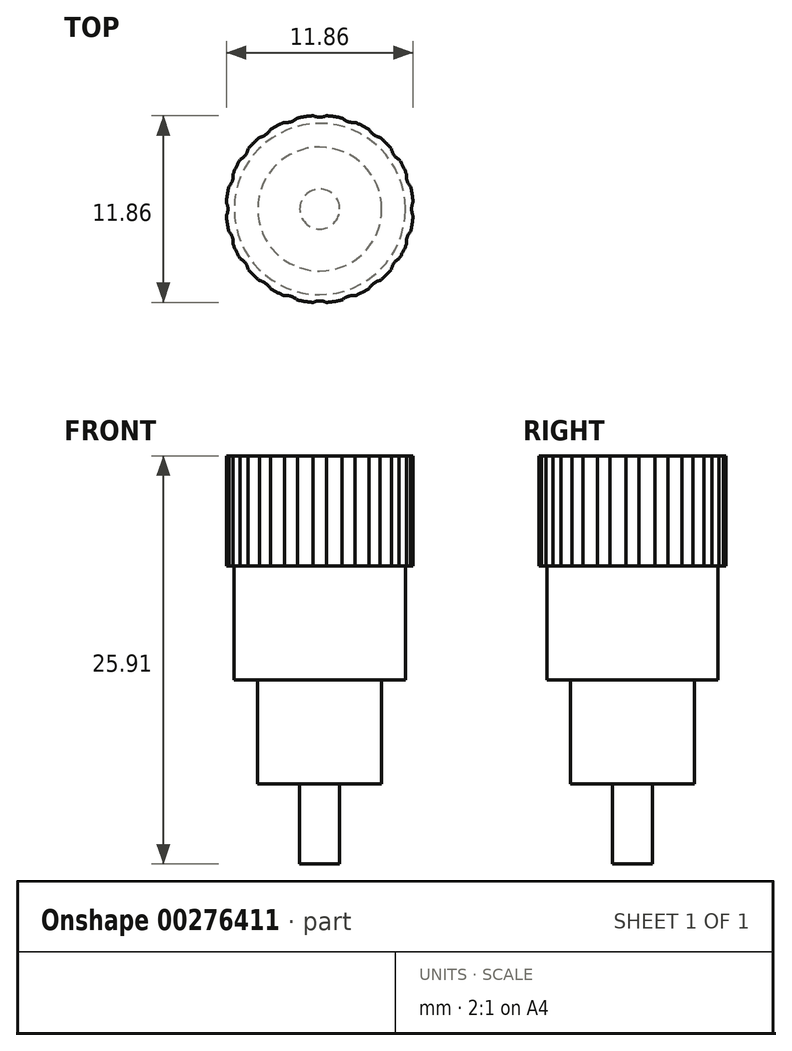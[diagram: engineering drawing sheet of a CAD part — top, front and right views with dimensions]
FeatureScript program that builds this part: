
annotation { "Feature Type Name" : "Feature", "Feature Type Description" : "" }
export const myFeature = defineFeature(function(context is Context, id is Id, definition is map)
    precondition{}
    {
        {
            var Q0;
            Q0=qCreatedBy(makeId("Front.planeOp"),FACE);
            var sketch = newSketch(context, id + "F0", { "sketchPlane" : qUnion([Q0])});
            skLineSegment(sketch, "E0", {"start": v(0, -6.98) * mm, "end": v(0, 66.06) * mm, "construction": true});
            skLineSegment(sketch, "E1", {"start": v(0, 20.83) * mm, "end": v(5.94, 20.83) * mm});
            skLineSegment(sketch, "E2", {"start": v(5.94, 20.83) * mm, "end": v(5.94, 13.84) * mm});
            skLineSegment(sketch, "E3", {"start": v(5.94, 13.84) * mm, "end": v(5.44, 13.84) * mm});
            skLineSegment(sketch, "E4", {"start": v(5.44, 13.84) * mm, "end": v(5.44, 6.6) * mm});
            skLineSegment(sketch, "E5", {"start": v(5.44, 6.6) * mm, "end": v(3.94, 6.6) * mm});
            skLineSegment(sketch, "E6", {"start": v(3.94, 6.6) * mm, "end": v(3.94, 0) * mm});
            skLineSegment(sketch, "E7", {"start": v(3.94, 0) * mm, "end": v(1.27, 0) * mm});
            skLineSegment(sketch, "E8", {"start": v(1.27, 0) * mm, "end": v(1.27, -5.08) * mm});
            skLineSegment(sketch, "E9", {"start": v(1.27, -5.08) * mm, "end": v(0, -5.08) * mm});
            skLineSegment(sketch, "E10", {"start": v(0, -5.08) * mm, "end": v(0, 20.83) * mm});
            skSolve(sketch);
        }
        {
            var Q0;
            Q0 = qSketchRegion(id + "F0", true);
            var Q1;
            Q1=sQuery(id+"F0.wireOp",EDGE,"E0");
            revolve(context, id + "F1", {"entities" : qUnion([Q0]), "axis" : qUnion([Q1]), "revolveType" : RevolveType.FULL});
        }
        {
            var Q0;
            Q0=makeQuery(id+"F1.opRevolve","SWEPT_FACE",FACE,{"disambiguationData":[OSD([sQuery(id+"F0.wireOp",EDGE,"E1")])]});
            var sketch = newSketch(context, id + "F2", { "sketchPlane" : qUnion([Q0])});
            skArc(sketch, "E11", {"start": v(0.43, 5.93) * mm, "mid": v(0, 5.83) * mm, "end": v(-0.43, 5.93) * mm});
            skArc(sketch, "E12", {"start": v(-0.43, 5.93) * mm, "mid": v(0, 5.94) * mm, "end": v(0.43, 5.93) * mm});
            skArc(sketch, "E13.1.0", {"start": v(-2.24, 5.5) * mm, "mid": v(-1.84, 5.65) * mm, "end": v(-1.43, 5.77) * mm});
            skArc(sketch, "E13.1.1", {"start": v(-1.43, 5.77) * mm, "mid": v(-1.8, 5.55) * mm, "end": v(-2.24, 5.5) * mm});
            skArc(sketch, "E13.2.0", {"start": v(-3.83, 4.54) * mm, "mid": v(-3.5, 4.8) * mm, "end": v(-3.14, 5.05) * mm});
            skArc(sketch, "E13.2.1", {"start": v(-3.14, 5.05) * mm, "mid": v(-3.43, 4.72) * mm, "end": v(-3.83, 4.54) * mm});
            skArc(sketch, "E13.3.0", {"start": v(-5.05, 3.14) * mm, "mid": v(-4.8, 3.5) * mm, "end": v(-4.54, 3.83) * mm});
            skArc(sketch, "E13.3.1", {"start": v(-4.54, 3.83) * mm, "mid": v(-4.72, 3.43) * mm, "end": v(-5.05, 3.14) * mm});
            skArc(sketch, "E13.4.0", {"start": v(-5.77, 1.43) * mm, "mid": v(-5.65, 1.84) * mm, "end": v(-5.5, 2.24) * mm});
            skArc(sketch, "E13.4.1", {"start": v(-5.5, 2.24) * mm, "mid": v(-5.55, 1.8) * mm, "end": v(-5.77, 1.43) * mm});
            skArc(sketch, "E13.5.0", {"start": v(-5.93, -0.43) * mm, "mid": v(-5.94, 0) * mm, "end": v(-5.93, 0.43) * mm});
            skArc(sketch, "E13.5.1", {"start": v(-5.93, 0.43) * mm, "mid": v(-5.83, 0) * mm, "end": v(-5.93, -0.43) * mm});
            skArc(sketch, "E13.6.0", {"start": v(-5.5, -2.24) * mm, "mid": v(-5.65, -1.84) * mm, "end": v(-5.77, -1.43) * mm});
            skArc(sketch, "E13.6.1", {"start": v(-5.77, -1.43) * mm, "mid": v(-5.55, -1.8) * mm, "end": v(-5.5, -2.24) * mm});
            skArc(sketch, "E13.7.0", {"start": v(-4.54, -3.83) * mm, "mid": v(-4.8, -3.5) * mm, "end": v(-5.05, -3.14) * mm});
            skArc(sketch, "E13.7.1", {"start": v(-5.05, -3.14) * mm, "mid": v(-4.72, -3.43) * mm, "end": v(-4.54, -3.83) * mm});
            skArc(sketch, "E13.8.0", {"start": v(-3.14, -5.05) * mm, "mid": v(-3.5, -4.8) * mm, "end": v(-3.83, -4.54) * mm});
            skArc(sketch, "E13.8.1", {"start": v(-3.83, -4.54) * mm, "mid": v(-3.43, -4.72) * mm, "end": v(-3.14, -5.05) * mm});
            skArc(sketch, "E13.9.0", {"start": v(-1.43, -5.77) * mm, "mid": v(-1.84, -5.65) * mm, "end": v(-2.24, -5.5) * mm});
            skArc(sketch, "E13.9.1", {"start": v(-2.24, -5.5) * mm, "mid": v(-1.8, -5.55) * mm, "end": v(-1.43, -5.77) * mm});
            skArc(sketch, "E13.10.0", {"start": v(0.43, -5.93) * mm, "mid": v(0, -5.94) * mm, "end": v(-0.43, -5.93) * mm});
            skArc(sketch, "E13.10.1", {"start": v(-0.43, -5.93) * mm, "mid": v(0, -5.83) * mm, "end": v(0.43, -5.93) * mm});
            skArc(sketch, "E13.11.0", {"start": v(2.24, -5.5) * mm, "mid": v(1.84, -5.65) * mm, "end": v(1.43, -5.77) * mm});
            skArc(sketch, "E13.11.1", {"start": v(1.43, -5.77) * mm, "mid": v(1.8, -5.55) * mm, "end": v(2.24, -5.5) * mm});
            skArc(sketch, "E13.12.0", {"start": v(3.83, -4.54) * mm, "mid": v(3.5, -4.8) * mm, "end": v(3.14, -5.05) * mm});
            skArc(sketch, "E13.12.1", {"start": v(3.14, -5.05) * mm, "mid": v(3.43, -4.72) * mm, "end": v(3.83, -4.54) * mm});
            skArc(sketch, "E13.13.0", {"start": v(5.05, -3.14) * mm, "mid": v(4.8, -3.5) * mm, "end": v(4.54, -3.83) * mm});
            skArc(sketch, "E13.13.1", {"start": v(4.54, -3.83) * mm, "mid": v(4.72, -3.43) * mm, "end": v(5.05, -3.14) * mm});
            skArc(sketch, "E13.14.0", {"start": v(5.77, -1.43) * mm, "mid": v(5.65, -1.84) * mm, "end": v(5.5, -2.24) * mm});
            skArc(sketch, "E13.14.1", {"start": v(5.5, -2.24) * mm, "mid": v(5.55, -1.8) * mm, "end": v(5.77, -1.43) * mm});
            skArc(sketch, "E13.15.0", {"start": v(5.93, 0.43) * mm, "mid": v(5.94, 0) * mm, "end": v(5.93, -0.43) * mm});
            skArc(sketch, "E13.15.1", {"start": v(5.93, -0.43) * mm, "mid": v(5.83, 0) * mm, "end": v(5.93, 0.43) * mm});
            skArc(sketch, "E13.16.0", {"start": v(5.5, 2.24) * mm, "mid": v(5.65, 1.84) * mm, "end": v(5.77, 1.43) * mm});
            skArc(sketch, "E13.16.1", {"start": v(5.77, 1.43) * mm, "mid": v(5.55, 1.8) * mm, "end": v(5.5, 2.24) * mm});
            skArc(sketch, "E13.17.0", {"start": v(4.54, 3.83) * mm, "mid": v(4.8, 3.5) * mm, "end": v(5.05, 3.14) * mm});
            skArc(sketch, "E13.17.1", {"start": v(5.05, 3.14) * mm, "mid": v(4.72, 3.43) * mm, "end": v(4.54, 3.83) * mm});
            skArc(sketch, "E13.18.0", {"start": v(3.14, 5.05) * mm, "mid": v(3.5, 4.8) * mm, "end": v(3.83, 4.54) * mm});
            skArc(sketch, "E13.18.1", {"start": v(3.83, 4.54) * mm, "mid": v(3.43, 4.72) * mm, "end": v(3.14, 5.05) * mm});
            skArc(sketch, "E13.19.0", {"start": v(1.43, 5.77) * mm, "mid": v(1.84, 5.65) * mm, "end": v(2.24, 5.5) * mm});
            skArc(sketch, "E13.19.1", {"start": v(2.24, 5.5) * mm, "mid": v(1.8, 5.55) * mm, "end": v(1.43, 5.77) * mm});
            skSolve(sketch);
        }
        {
            var Q0;
            Q0 = qSketchRegion(id + "F2", true);
            extrude(context, id + "F3", {"entities" : qUnion([Q0]), "operationType" : NewBodyOperationType.REMOVE, "endBound" : BoundingType.THROUGH_ALL, "oppositeDirection" : true, "depth" : 25.4 * mm});
        }
    });
